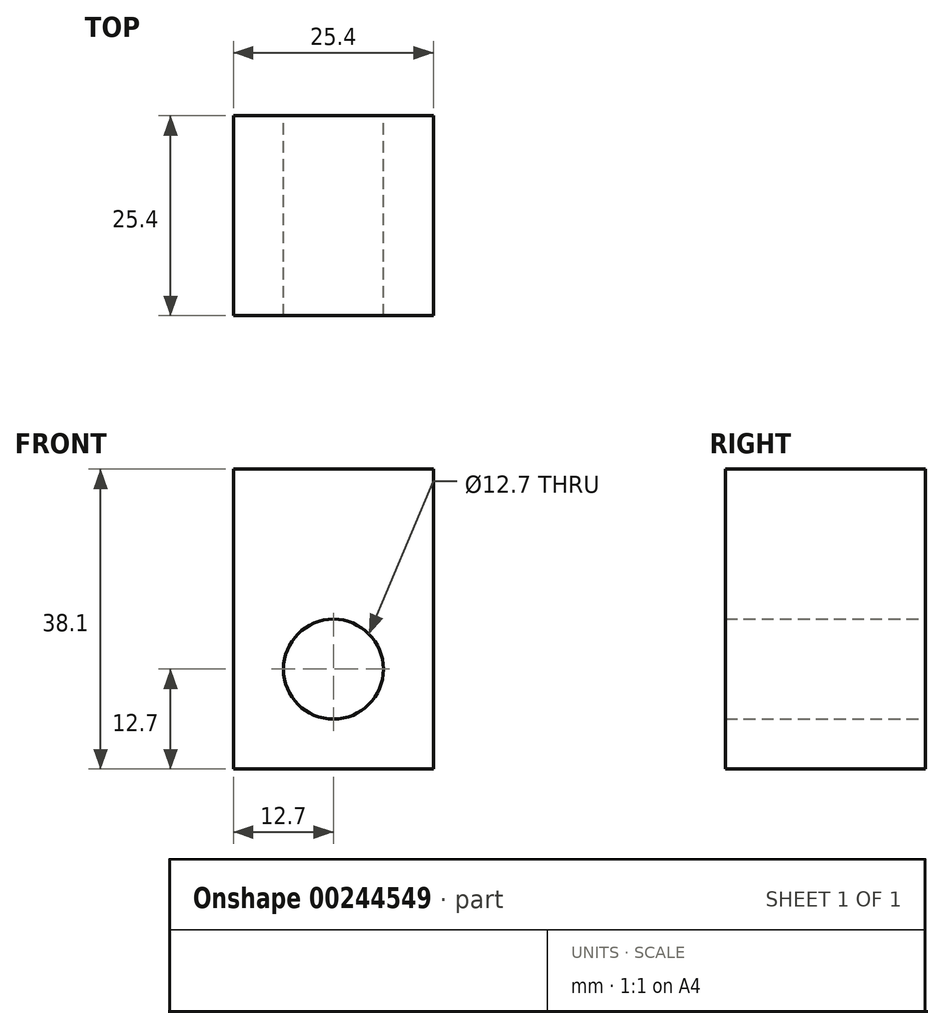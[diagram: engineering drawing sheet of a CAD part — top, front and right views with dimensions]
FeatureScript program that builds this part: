
annotation { "Feature Type Name" : "Feature", "Feature Type Description" : "" }
export const myFeature = defineFeature(function(context is Context, id is Id, definition is map)
    precondition{}
    {
        {
            var Q0;
            Q0=qCreatedBy(makeId("Top.planeOp"),FACE);
            var sketch = newSketch(context, id + "F0", { "sketchPlane" : qUnion([Q0])});
            skLineSegment(sketch, "E0", {"start": v(0, 0) * mm, "end": v(25.4, 0) * mm});
            skLineSegment(sketch, "E1", {"start": v(25.4, 0) * mm, "end": v(25.4, 25.4) * mm});
            skLineSegment(sketch, "E2", {"start": v(25.4, 25.4) * mm, "end": v(0, 25.4) * mm});
            skLineSegment(sketch, "E3", {"start": v(0, 25.4) * mm, "end": v(0, 0) * mm});
            skSolve(sketch);
        }
        {
            var Q0;
            Q0=makeQuery(id+"F0.imprint","IMPRINT",FACE,{"disambiguationData":[TD([[makeQuery(id+"F0.imprint","IMPRINT",EDGE,{"derivedFrom":sQuery(id+"F0.wireOp",EDGE,"E0")}),1.0]])]});
            extrude(context, id + "F1", {"entities" : qUnion([Q0]), "depth" : 38.1 * mm});
        }
        {
            var Q0;
            Q0=makeQuery(id+"F1.opExtrude","SWEPT_FACE",FACE,{"disambiguationData":[OSD([sQuery(id+"F0.wireOp",EDGE,"E2")])]});
            var sketch = newSketch(context, id + "F2", { "sketchPlane" : qUnion([Q0])});
            skCircle(sketch, "E4", {"center": v(-12.7, 12.7) * mm, "radius": 6.35 * mm});
            skSolve(sketch);
        }
        {
            var Q0;
            Q0=makeQuery(id+"F2.imprint","IMPRINT",FACE,{"disambiguationData":[TD([[makeQuery(id+"F2.imprint","IMPRINT",EDGE,{"derivedFrom":sQuery(id+"F2.wireOp",EDGE,"E4")}),1.0]])]});
            extrude(context, id + "F3", {"entities" : qUnion([Q0]), "operationType" : NewBodyOperationType.REMOVE, "endBound" : BoundingType.THROUGH_ALL, "oppositeDirection" : true, "depth" : 25.4 * mm});
        }
    });
